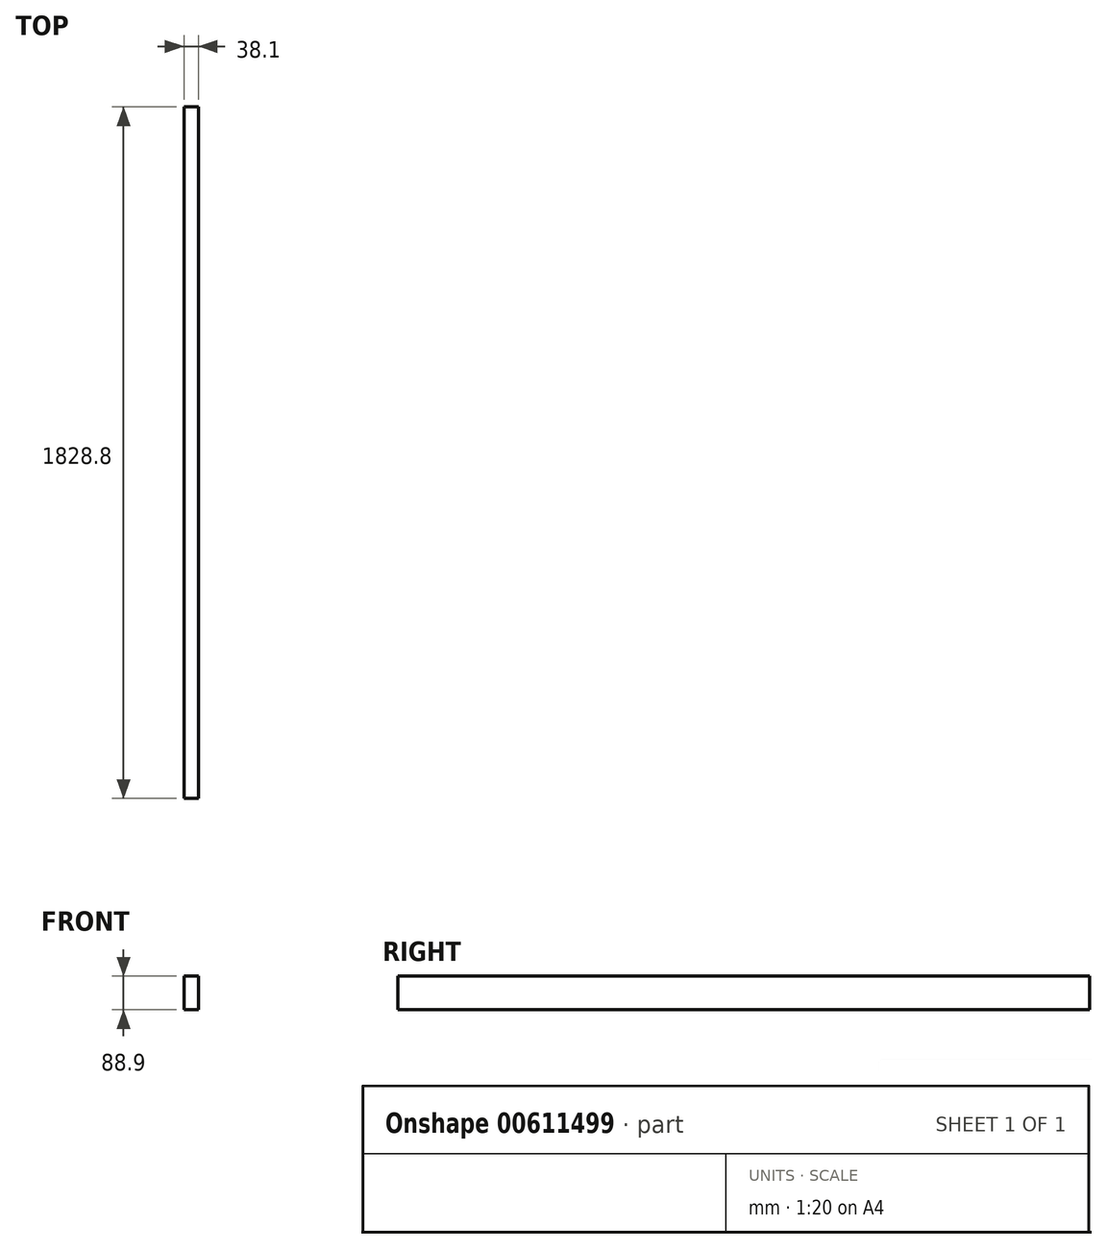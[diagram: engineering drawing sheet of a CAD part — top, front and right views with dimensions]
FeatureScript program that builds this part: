
annotation { "Feature Type Name" : "Feature", "Feature Type Description" : "" }
export const myFeature = defineFeature(function(context is Context, id is Id, definition is map)
    precondition{}
    {
        {
            var Q0;
            Q0=qCreatedBy(makeId("Front.planeOp"),FACE);
            var sketch = newSketch(context, id + "F0", { "sketchPlane" : qUnion([Q0])});
            skLineSegment(sketch, "E0.bottom", {"start": v(-21.25, 77.69) * mm, "end": v(16.85, 77.69) * mm});
            skLineSegment(sketch, "E0.top", {"start": v(-21.25, -11.21) * mm, "end": v(16.85, -11.21) * mm});
            skLineSegment(sketch, "E0.left", {"start": v(-21.25, 77.69) * mm, "end": v(-21.25, -11.21) * mm});
            skLineSegment(sketch, "E0.right", {"start": v(16.85, 77.69) * mm, "end": v(16.85, -11.21) * mm});
            skSolve(sketch);
        }
        {
            var Q0;
            Q0=makeQuery(id+"F0.imprint","IMPRINT",FACE,{"disambiguationData":[TD([[makeQuery(id+"F0.imprint","IMPRINT",EDGE,{"derivedFrom":sQuery(id+"F0.wireOp",EDGE,"E0.bottom")}),-1.0]])]});
            extrude(context, id + "F1", {"entities" : qUnion([Q0]), "depth" : 1828.8 * mm, "offsetDistance" : 25.4 * mm});
        }
    });
